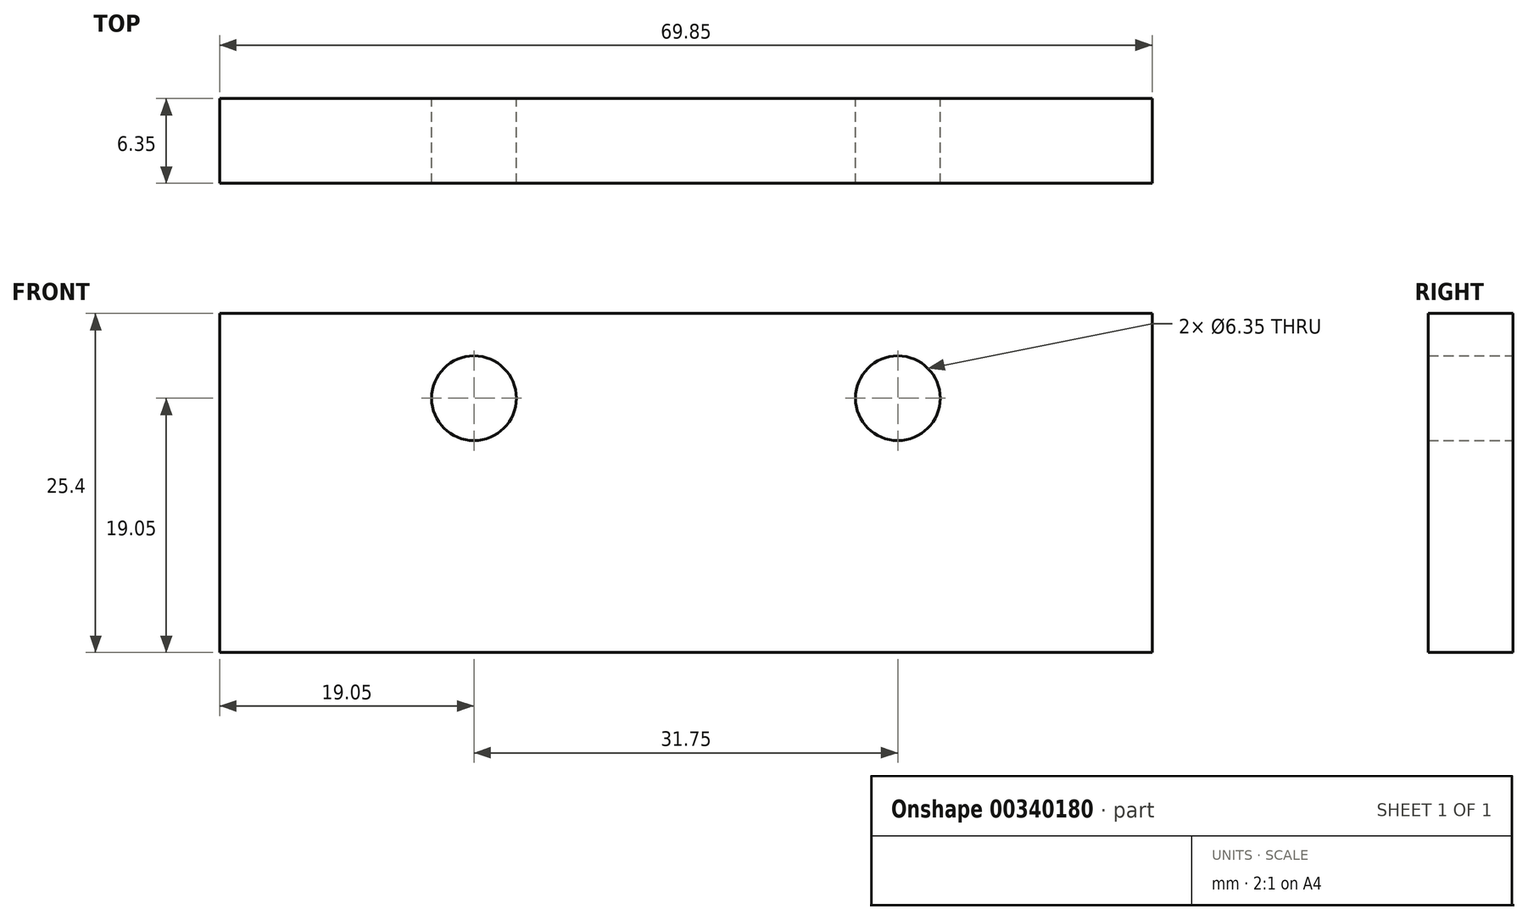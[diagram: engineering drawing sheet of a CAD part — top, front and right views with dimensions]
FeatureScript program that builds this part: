
annotation { "Feature Type Name" : "Feature", "Feature Type Description" : "" }
export const myFeature = defineFeature(function(context is Context, id is Id, definition is map)
    precondition{}
    {
        {
            var Q0;
            Q0=qCreatedBy(makeId("Front.planeOp"),FACE);
            var sketch = newSketch(context, id + "F0", { "sketchPlane" : qUnion([Q0])});
            skLineSegment(sketch, "E0.bottom", {"start": v(0, 0) * mm, "end": v(69.85, 0) * mm});
            skLineSegment(sketch, "E0.top", {"start": v(0, 25.4) * mm, "end": v(69.85, 25.4) * mm});
            skLineSegment(sketch, "E0.left", {"start": v(0, 0) * mm, "end": v(0, 25.4) * mm});
            skLineSegment(sketch, "E0.right", {"start": v(69.85, 0) * mm, "end": v(69.85, 25.4) * mm});
            skCircle(sketch, "E1", {"center": v(19.05, 19.05) * mm, "radius": 3.18 * mm});
            skCircle(sketch, "E2", {"center": v(50.8, 19.05) * mm, "radius": 3.18 * mm});
            skSolve(sketch);
        }
        {
            var Q0;
            Q0 = qSketchRegion(id + "F0", true);
            extrude(context, id + "F1", {"entities" : qUnion([Q0]), "depth" : 6.35 * mm});
        }
    });
